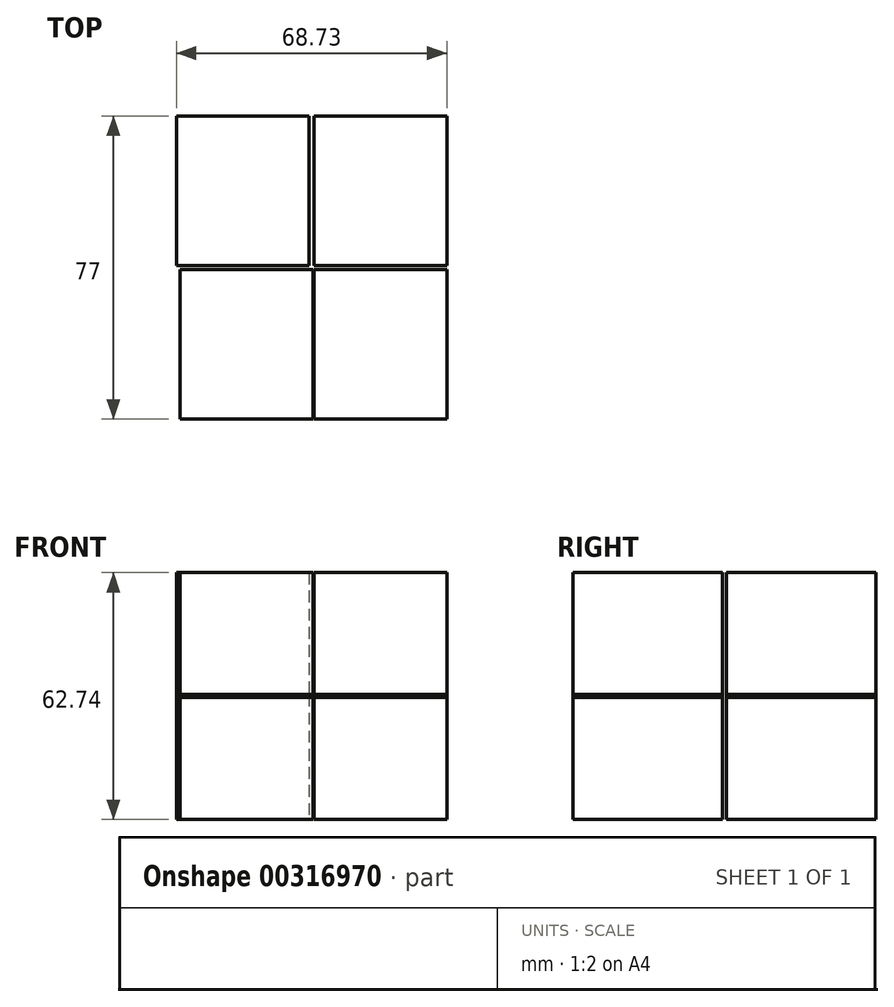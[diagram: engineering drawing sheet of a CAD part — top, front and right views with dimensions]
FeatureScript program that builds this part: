
annotation { "Feature Type Name" : "Feature", "Feature Type Description" : "" }
export const myFeature = defineFeature(function(context is Context, id is Id, definition is map)
    precondition{}
    {
        {
            var Q0;
            Q0=qCreatedBy(makeId("Front.planeOp"),FACE);
            var sketch = newSketch(context, id + "F0", { "sketchPlane" : qUnion([Q0])});
            skLineSegment(sketch, "E0.bottom", {"start": v(-33.73, 31.74) * mm, "end": v(0, 31.74) * mm});
            skLineSegment(sketch, "E0.top", {"start": v(-33.73, 0) * mm, "end": v(0, 0) * mm});
            skLineSegment(sketch, "E0.left", {"start": v(-33.73, 31.74) * mm, "end": v(-33.73, 0) * mm});
            skLineSegment(sketch, "E0.right", {"start": v(0, 31.74) * mm, "end": v(0, 0) * mm});
            skSolve(sketch);
        }
        {
            var Q0;
            Q0=makeQuery(id+"F0.imprint","IMPRINT",FACE,{"disambiguationData":[TD([[makeQuery(id+"F0.imprint","IMPRINT",EDGE,{"derivedFrom":sQuery(id+"F0.wireOp",EDGE,"E0.bottom")}),-1.0]])]});
            extrude(context, id + "F1", {"entities" : qUnion([Q0]), "depth" : 38 * mm});
        }
        {
            var Q0;
            Q0=makeQuery(id+"F1.opExtrude","SWEPT_BODY",BODY,{"disambiguationData":[OSD([sQuery(id+"F0.wireOp",EDGE,"E0.bottom"),sQuery(id+"F0.wireOp",EDGE,"E0.top"),sQuery(id+"F0.wireOp",EDGE,"E0.left"),sQuery(id+"F0.wireOp",EDGE,"E0.right")])]});
            transform(context, id + "F2", {"entities" : qUnion([Q0]), "transformType" : TransformType.TRANSLATION_3D, "dx" : 34 * mm, "dy" : 0 * mm, "dz" : 0 * mm, "makeCopy" : true});
        }
        {
            var Q0;
            Q0=makeQuery(id+"F2.opPattern","COPY",BODY,{"derivedFrom":makeQuery(id+"F1.opExtrude","SWEPT_BODY",BODY,{"disambiguationData":[OSD([sQuery(id+"F0.wireOp",EDGE,"E0.bottom"),sQuery(id+"F0.wireOp",EDGE,"E0.top"),sQuery(id+"F0.wireOp",EDGE,"E0.left"),sQuery(id+"F0.wireOp",EDGE,"E0.right")])]}),"instanceName":"1"});
            transform(context, id + "F3", {"entities" : qUnion([Q0]), "transformType" : TransformType.TRANSLATION_3D, "dx" : 0 * mm, "dy" : 0 * mm, "dz" : 31 * mm, "makeCopy" : true});
        }
        {
            var Q0;
            Q0=makeQuery(id+"F2.opPattern","COPY",BODY,{"derivedFrom":makeQuery(id+"F1.opExtrude","SWEPT_BODY",BODY,{"disambiguationData":[OSD([sQuery(id+"F0.wireOp",EDGE,"E0.bottom"),sQuery(id+"F0.wireOp",EDGE,"E0.top"),sQuery(id+"F0.wireOp",EDGE,"E0.left"),sQuery(id+"F0.wireOp",EDGE,"E0.right")])]}),"instanceName":"1"});
            transform(context, id + "F4", {"entities" : qUnion([Q0]), "transformType" : TransformType.TRANSLATION_3D, "dx" : 0 * mm, "dy" : 39 * mm, "dz" : 0 * mm, "makeCopy" : true});
        }
        {
            var Q0;
            Q0=makeQuery(id+"F4.opPattern","COPY",BODY,{"derivedFrom":makeQuery(id+"F2.opPattern","COPY",BODY,{"derivedFrom":makeQuery(id+"F1.opExtrude","SWEPT_BODY",BODY,{"disambiguationData":[OSD([sQuery(id+"F0.wireOp",EDGE,"E0.bottom"),sQuery(id+"F0.wireOp",EDGE,"E0.top"),sQuery(id+"F0.wireOp",EDGE,"E0.left"),sQuery(id+"F0.wireOp",EDGE,"E0.right")])]}),"instanceName":"1"}),"instanceName":"1"});
            transform(context, id + "F5", {"entities" : qUnion([Q0]), "transformType" : TransformType.TRANSLATION_3D, "dx" : -35 * mm, "dy" : 0 * mm, "dz" : 0 * mm, "makeCopy" : true});
        }
        {
            var Q0;
            Q0=makeQuery(id+"F4.opPattern","COPY",BODY,{"derivedFrom":makeQuery(id+"F2.opPattern","COPY",BODY,{"derivedFrom":makeQuery(id+"F1.opExtrude","SWEPT_BODY",BODY,{"disambiguationData":[OSD([sQuery(id+"F0.wireOp",EDGE,"E0.bottom"),sQuery(id+"F0.wireOp",EDGE,"E0.top"),sQuery(id+"F0.wireOp",EDGE,"E0.left"),sQuery(id+"F0.wireOp",EDGE,"E0.right")])]}),"instanceName":"1"}),"instanceName":"1"});
            transform(context, id + "F6", {"entities" : qUnion([Q0]), "transformType" : TransformType.TRANSLATION_3D, "dx" : 0 * mm, "dy" : 0 * mm, "dz" : 31 * mm, "makeCopy" : true});
        }
        {
            var Q0;
            Q0=makeQuery(id+"F5.opPattern","COPY",BODY,{"derivedFrom":makeQuery(id+"F4.opPattern","COPY",BODY,{"derivedFrom":makeQuery(id+"F2.opPattern","COPY",BODY,{"derivedFrom":makeQuery(id+"F1.opExtrude","SWEPT_BODY",BODY,{"disambiguationData":[OSD([sQuery(id+"F0.wireOp",EDGE,"E0.bottom"),sQuery(id+"F0.wireOp",EDGE,"E0.top"),sQuery(id+"F0.wireOp",EDGE,"E0.left"),sQuery(id+"F0.wireOp",EDGE,"E0.right")])]}),"instanceName":"1"}),"instanceName":"1"}),"instanceName":"1"});
            var Q1;
            Q1=makeQuery(id+"F1.opExtrude","SWEPT_BODY",BODY,{"disambiguationData":[OSD([sQuery(id+"F0.wireOp",EDGE,"E0.bottom"),sQuery(id+"F0.wireOp",EDGE,"E0.top"),sQuery(id+"F0.wireOp",EDGE,"E0.left"),sQuery(id+"F0.wireOp",EDGE,"E0.right")])]});
            transform(context, id + "F7", {"entities" : qUnion([Q0, Q1]), "transformType" : TransformType.TRANSLATION_3D, "dx" : 0 * mm, "dy" : 0 * mm, "dz" : 31 * mm, "makeCopy" : true});
        }
    });
